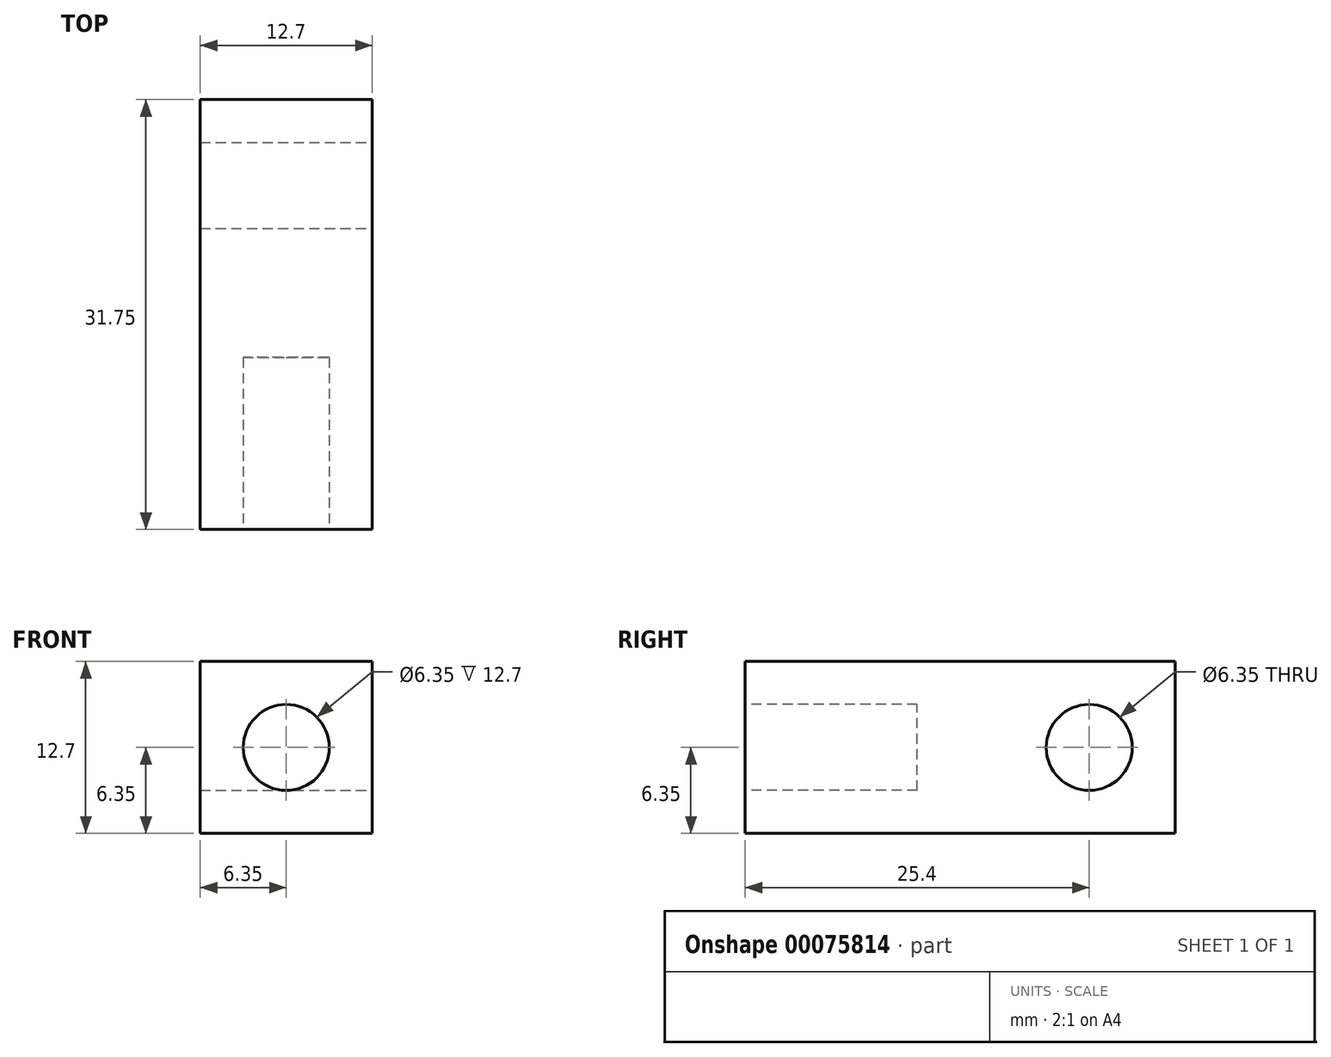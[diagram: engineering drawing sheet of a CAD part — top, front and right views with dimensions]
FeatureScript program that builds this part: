
annotation { "Feature Type Name" : "Feature", "Feature Type Description" : "" }
export const myFeature = defineFeature(function(context is Context, id is Id, definition is map)
    precondition{}
    {
        {
            var Q0;
            Q0=qCreatedBy(makeId("Front.planeOp"),FACE);
            var sketch = newSketch(context, id + "F0", { "sketchPlane" : qUnion([Q0])});
            skLineSegment(sketch, "E0.bottom", {"start": v(6.35, -6.35) * mm, "end": v(-6.35, -6.35) * mm});
            skLineSegment(sketch, "E0.top", {"start": v(6.35, 6.35) * mm, "end": v(-6.35, 6.35) * mm});
            skLineSegment(sketch, "E0.left", {"start": v(6.35, -6.35) * mm, "end": v(6.35, 6.35) * mm});
            skLineSegment(sketch, "E0.right", {"start": v(-6.35, -6.35) * mm, "end": v(-6.35, 6.35) * mm});
            skPoint(sketch, "E0.middle", {"position": v(0, 0) * mm});
            skSolve(sketch);
        }
        {
            var Q0;
            Q0 = qSketchRegion(id + "F0", true);
            extrude(context, id + "F1", {"entities" : qUnion([Q0]), "oppositeDirection" : true, "depth" : 31.75 * mm});
        }
        {
            var Q0;
            Q0=makeQuery(id+"F1.opExtrude","CAP_FACE",FACE,{"disambiguationData":[OSD([sQuery(id+"F0.wireOp",EDGE,"E0.bottom"),sQuery(id+"F0.wireOp",EDGE,"E0.top"),sQuery(id+"F0.wireOp",EDGE,"E0.left"),sQuery(id+"F0.wireOp",EDGE,"E0.right")])],"isStart":true});
            var sketch = newSketch(context, id + "F2", { "sketchPlane" : qUnion([Q0])});
            skCircle(sketch, "E1", {"center": v(0, 0) * mm, "radius": 3.18 * mm});
            skSolve(sketch);
        }
        {
            var Q0;
            Q0 = qSketchRegion(id + "F2", true);
            extrude(context, id + "F3", {"entities" : qUnion([Q0]), "operationType" : NewBodyOperationType.REMOVE, "oppositeDirection" : true, "depth" : 12.7 * mm});
        }
        {
            var Q0;
            Q0=makeQuery(id+"F1.opExtrude","SWEPT_FACE",FACE,{"disambiguationData":[OSD([sQuery(id+"F0.wireOp",EDGE,"E0.left")])]});
            var sketch = newSketch(context, id + "F4", { "sketchPlane" : qUnion([Q0])});
            skCircle(sketch, "E2", {"center": v(25.4, 0) * mm, "radius": 3.17 * mm});
            skPoint(sketch, "E2.centerSnap0", {"position": v(31.75, 0) * mm});
            skSolve(sketch);
        }
        {
            var Q0;
            Q0 = qSketchRegion(id + "F4", true);
            extrude(context, id + "F5", {"entities" : qUnion([Q0]), "operationType" : NewBodyOperationType.REMOVE, "endBound" : BoundingType.THROUGH_ALL, "oppositeDirection" : true, "depth" : 25 * mm});
        }
    });
